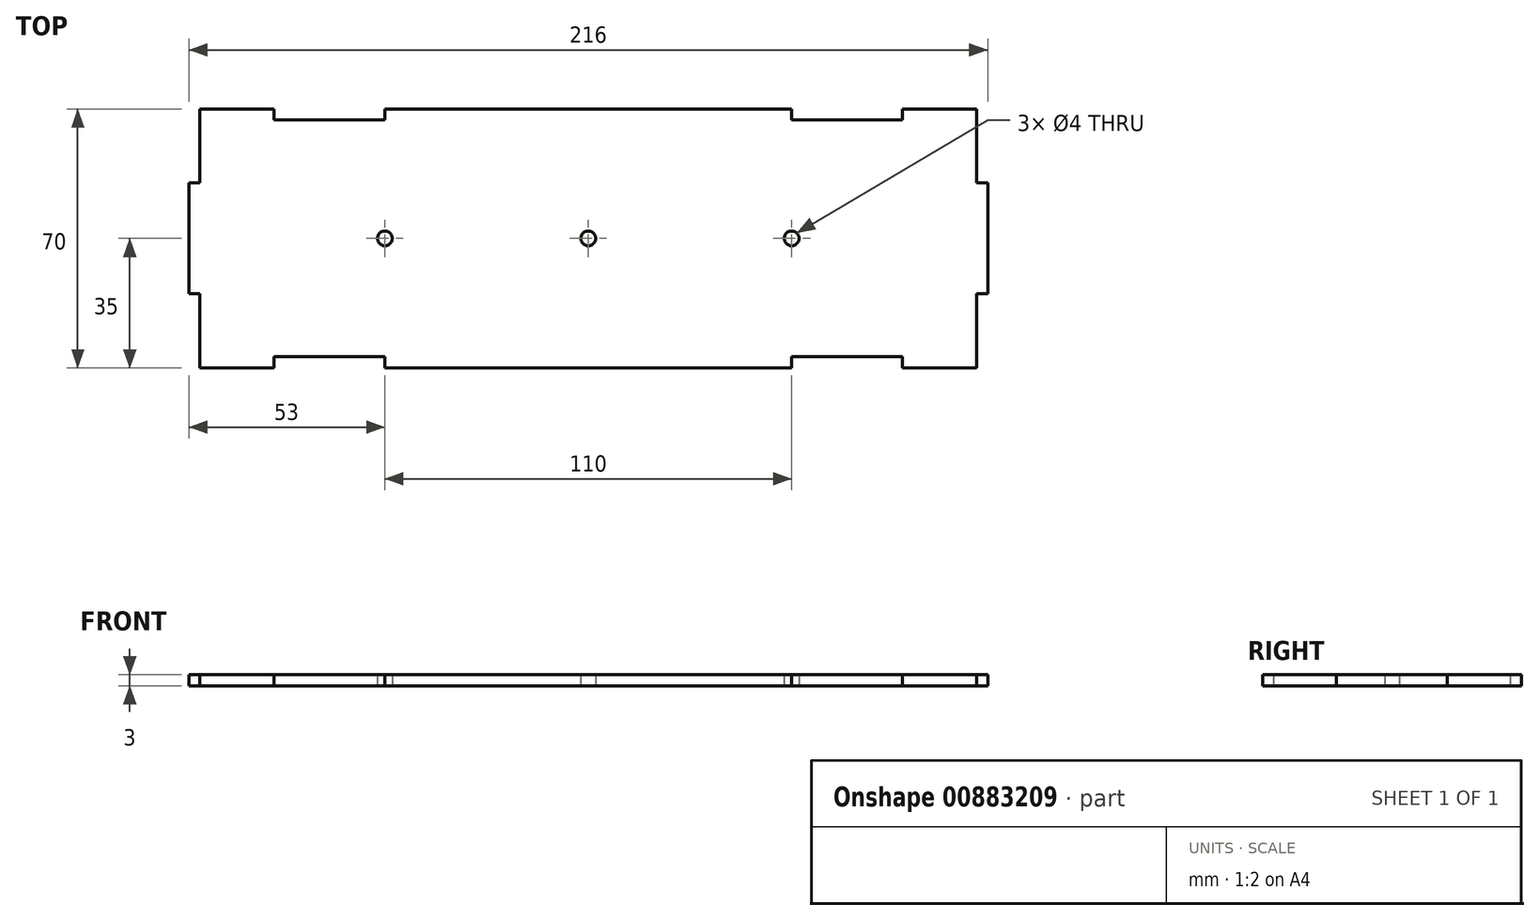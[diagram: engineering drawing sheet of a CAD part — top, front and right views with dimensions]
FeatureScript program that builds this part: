
annotation { "Feature Type Name" : "Feature", "Feature Type Description" : "" }
export const myFeature = defineFeature(function(context is Context, id is Id, definition is map)
    precondition{}
    {
        {
            var Q0;
            Q0=qCreatedBy(makeId("Top.planeOp"),FACE);
            var sketch = newSketch(context, id + "F0", { "sketchPlane" : qUnion([Q0])});
            skLineSegment(sketch, "E0.bottom", {"start": v(0, 0) * mm, "end": v(210, 0) * mm});
            skLineSegment(sketch, "E0.top", {"start": v(0, 70) * mm, "end": v(210, 70) * mm});
            skLineSegment(sketch, "E0.left", {"start": v(0, 0) * mm, "end": v(0, 70) * mm});
            skLineSegment(sketch, "E0.right", {"start": v(210, 0) * mm, "end": v(210, 70) * mm});
            skLineSegment(sketch, "E1", {"start": v(210, 50) * mm, "end": v(213, 50) * mm});
            skLineSegment(sketch, "E2", {"start": v(213, 50) * mm, "end": v(213, 20) * mm});
            skLineSegment(sketch, "E3", {"start": v(213, 20) * mm, "end": v(210, 20) * mm});
            skLineSegment(sketch, "E4", {"start": v(0, 50) * mm, "end": v(-3, 50) * mm});
            skLineSegment(sketch, "E5", {"start": v(-3, 50) * mm, "end": v(-3, 20) * mm});
            skLineSegment(sketch, "E6", {"start": v(-3, 20) * mm, "end": v(0, 20) * mm});
            skLineSegment(sketch, "E7", {"start": v(20, 0) * mm, "end": v(20, 3) * mm});
            skLineSegment(sketch, "E8", {"start": v(20, 3) * mm, "end": v(50, 3) * mm});
            skLineSegment(sketch, "E9", {"start": v(50, 3) * mm, "end": v(50, 0) * mm});
            skLineSegment(sketch, "E10", {"start": v(160, 0) * mm, "end": v(160, 3) * mm});
            skLineSegment(sketch, "E11", {"start": v(160, 3) * mm, "end": v(190, 3) * mm});
            skLineSegment(sketch, "E12", {"start": v(190, 3) * mm, "end": v(190, 0) * mm});
            skLineSegment(sketch, "E13", {"start": v(190, 70) * mm, "end": v(190, 67) * mm});
            skLineSegment(sketch, "E14", {"start": v(190, 67) * mm, "end": v(160, 67) * mm});
            skLineSegment(sketch, "E15", {"start": v(160, 67) * mm, "end": v(160, 70) * mm});
            skLineSegment(sketch, "E16", {"start": v(50, 70) * mm, "end": v(50, 67) * mm});
            skLineSegment(sketch, "E17", {"start": v(50, 67) * mm, "end": v(20, 67) * mm});
            skLineSegment(sketch, "E18", {"start": v(20, 67) * mm, "end": v(20, 70) * mm});
            skCircle(sketch, "E19", {"center": v(105, 35) * mm, "radius": 2 * mm});
            skPoint(sketch, "E20", {"position": v(105, 70) * mm});
            skPoint(sketch, "E21", {"position": v(0, 35) * mm});
            skCircle(sketch, "E22", {"center": v(160, 35) * mm, "radius": 2 * mm});
            skCircle(sketch, "E23", {"center": v(50, 35) * mm, "radius": 2 * mm});
            skSolve(sketch);
        }
        {
            var Q0;
            {var subQ0=sQuery(id+"F0.wireOp",EDGE,"E4");Q0=makeQuery(id+"F0.imprint","IMPRINT",FACE,{"disambiguationData":[TD([[makeQuery(id+"F0.imprint","IMPRINT",EDGE,{"derivedFrom":subQ0}),1.0]])]});}
            var Q1;
            {var subQ0=sQuery(id+"F0.wireOp",EDGE,"E1");Q1=makeQuery(id+"F0.imprint","IMPRINT",FACE,{"disambiguationData":[TD([[makeQuery(id+"F0.imprint","IMPRINT",EDGE,{"derivedFrom":subQ0}),-1.0]])]});}
            var Q2;
            {var subQ6=sQuery(id+"F0.wireOp",EDGE,"E0.top");Q2=makeQuery(id+"F0.imprint","IMPRINT",FACE,{"disambiguationData":[TD([[makeQuery(id+"F0.imprint","IMPRINT",EDGE,{"derivedFrom":subQ6}),-1.0]])]});}
            extrude(context, id + "F1", {"entities" : qUnion([Q0, Q1, Q2]), "depth" : 3 * mm, "offsetDistance" : 25 * mm});
        }
    });
